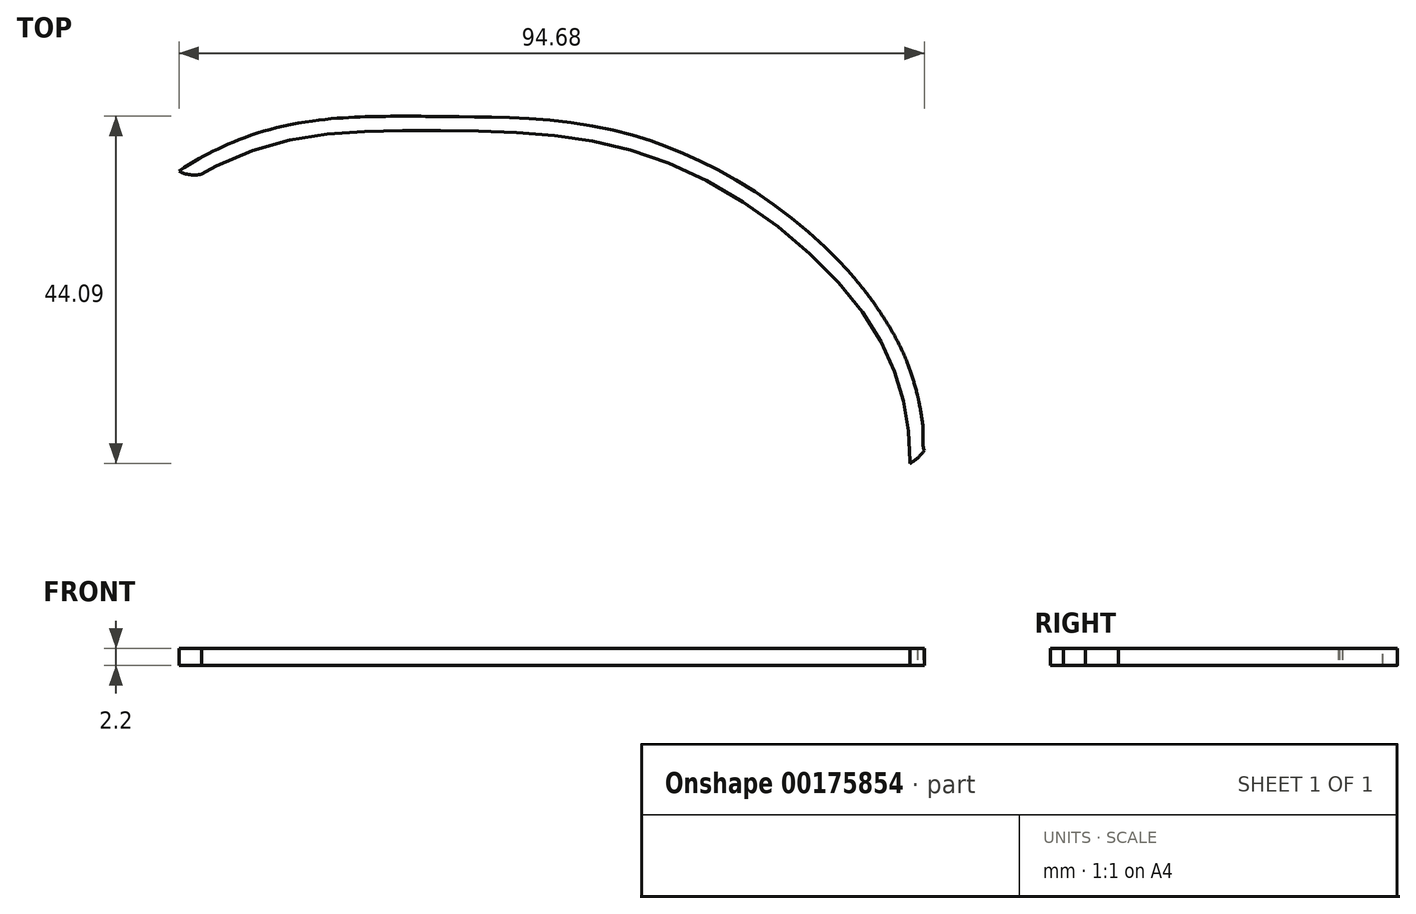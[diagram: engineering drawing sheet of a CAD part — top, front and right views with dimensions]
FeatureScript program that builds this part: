
annotation { "Feature Type Name" : "Feature", "Feature Type Description" : "" }
export const myFeature = defineFeature(function(context is Context, id is Id, definition is map)
    precondition{}
    {
        {
            var Q0;
            Q0=qCreatedBy(makeId("Top.planeOp"),FACE);
            var sketch = newSketch(context, id + "F0", { "sketchPlane" : qUnion([Q0])});
            skLineSegment(sketch, "E0.bottom", {"start": v(-2.66, 38.82) * mm, "end": v(-2.66, 38.82) * mm});
            skLineSegment(sketch, "E0.top", {"start": v(-2.66, -45.18) * mm, "end": v(-2.66, -45.18) * mm});
            skLineSegment(sketch, "E0.left", {"start": v(-62.96, 0) * mm, "end": v(-62.96, -6.37) * mm});
            skPoint(sketch, "E1", {"position": v(116.17, -2.24) * mm});
            skPoint(sketch, "E2", {"position": v(57.5, -3.18) * mm});
            skLineSegment(sketch, "E3", {"start": v(89.29, -3.18) * mm, "end": v(-122.26, -3.18) * mm, "construction": true});
            skFitSpline(sketch, "E4", {"points": [v(57.5, -3.18) * mm, v(51.83, 15.26) * mm, v(26.1, 35.01) * mm, v(-2.66, 38.82) * mm, v(-30.61, 34.33) * mm, v(-55.45, 11.12) * mm, v(-62.96, 0) * mm], "startDerivative": vector(0, 129.1) * mm, "endDerivative": vector(-47.35, -84.57) * mm});
            skFitSpline(sketch, "E5.MirrorCS", {"points": [v(57.5, -3.18) * mm, v(51.83, -21.63) * mm, v(26.1, -41.38) * mm, v(-2.66, -45.18) * mm, v(-30.61, -40.7) * mm, v(-55.45, -17.5) * mm, v(-62.96, -6.37) * mm], "startDerivative": vector(0, -129.1) * mm, "endDerivative": vector(-47.35, 84.57) * mm});
            skPoint(sketch, "E6.orphan", {"position": v(-62.96, 38.82) * mm});
            skPoint(sketch, "E7.orphan", {"position": v(57.63, 38.82) * mm});
            skPoint(sketch, "E8.orphan", {"position": v(57.37, -45.18) * mm});
            skFitSpline(sketch, "E9.0", {"points": [v(59.33, -3.18) * mm, v(59.33, -1.78) * mm, v(59.18, 1.03) * mm, v(58.46, 5.25) * mm, v(57.13, 9.45) * mm, v(55.46, 12.94) * mm, v(53.76, 15.71) * mm, v(51.79, 18.47) * mm, v(48.88, 21.87) * mm, v(44.8, 25.76) * mm, v(40.25, 29.38) * mm, v(35.35, 32.6) * mm, v(31.07, 34.9) * mm, v(27.59, 36.42) * mm, v(24.09, 37.72) * mm, v(19.72, 38.92) * mm, v(14.5, 39.84) * mm, v(9.33, 40.34) * mm, v(5.06, 40.53) * mm, v(1.66, 40.6) * mm, v(-0.88, 40.62) * mm, v(-3.4, 40.64) * mm, v(-5.95, 40.66) * mm, v(-8.5, 40.65) * mm, v(-11.9, 40.58) * mm, v(-16.2, 40.33) * mm, v(-21.36, 39.57) * mm, v(-25.65, 38.43) * mm, v(-29.06, 37.12) * mm, v(-31.6, 35.91) * mm, v(-34.11, 34.47) * mm, v(-37.38, 32.3) * mm, v(-41.32, 29.2) * mm, v(-45.76, 25.06) * mm, v(-49.84, 20.77) * mm, v(-53.49, 16.54) * mm, v(-56.63, 12.61) * mm, v(-59.17, 9.25) * mm, v(-61.95, 5.3) * mm, v(-63.54, 2.69) * mm, v(-64.55, 0.89) * mm]});
            skFitSpline(sketch, "E9.1", {"points": [v(59.33, -3.18) * mm, v(59.33, -4.59) * mm, v(59.18, -7.4) * mm, v(58.46, -11.62) * mm, v(57.13, -15.82) * mm, v(55.46, -19.3) * mm, v(53.76, -22.08) * mm, v(51.79, -24.84) * mm, v(48.88, -28.23) * mm, v(44.8, -32.13) * mm, v(40.25, -35.74) * mm, v(35.35, -38.97) * mm, v(31.07, -41.26) * mm, v(27.59, -42.78) * mm, v(24.09, -44.08) * mm, v(19.72, -45.29) * mm, v(14.5, -46.2) * mm, v(9.33, -46.7) * mm, v(5.06, -46.9) * mm, v(1.66, -46.96) * mm, v(-0.88, -47) * mm, v(-3.4, -47.01) * mm, v(-5.95, -47.03) * mm, v(-8.5, -47.02) * mm, v(-11.9, -46.95) * mm, v(-16.2, -46.7) * mm, v(-21.36, -45.94) * mm, v(-25.65, -44.8) * mm, v(-29.06, -43.48) * mm, v(-31.6, -42.28) * mm, v(-34.11, -40.84) * mm, v(-37.38, -38.67) * mm, v(-41.32, -35.56) * mm, v(-45.76, -31.43) * mm, v(-49.84, -27.13) * mm, v(-53.49, -22.9) * mm, v(-56.63, -18.98) * mm, v(-59.17, -15.62) * mm, v(-61.95, -11.67) * mm, v(-63.54, -9.05) * mm, v(-64.55, -7.26) * mm]});
            skLineSegment(sketch, "E10", {"start": v(-30.61, 34.33) * mm, "end": v(-31.63, 35.85) * mm});
            skLineSegment(sketch, "E11.MirrorCS", {"start": v(-30.61, -40.7) * mm, "end": v(-31.63, -42.22) * mm});
            skPoint(sketch, "E12.start.orphan", {"position": v(58.81, 3.06) * mm});
            skLineSegment(sketch, "E13.bottom", {"start": v(58.57, 4.32) * mm, "end": v(77.5, 4.32) * mm});
            skLineSegment(sketch, "E13.top", {"start": v(58.57, -10.68) * mm, "end": v(77.5, -10.68) * mm});
            skLineSegment(sketch, "E13.right", {"start": v(77.5, -0.18) * mm, "end": v(77.5, -6.18) * mm});
            skArc(sketch, "E14", {"start": v(77.5, -10.68) * mm, "mid": v(85, -3.18) * mm, "end": v(77.5, 4.32) * mm});
            skCircle(sketch, "E15", {"center": v(77.5, -3.18) * mm, "radius": 3 * mm});
            skArc(sketch, "E16", {"start": v(-33.05, 41.17) * mm, "mid": v(-37.18, 35.85) * mm, "end": v(-30.61, 34.33) * mm});
            skFitSpline(sketch, "E17", {"points": [v(-33.05, 41.17) * mm, v(-16.7, 40.2) * mm], "startDerivative": vector(14.5, -1.33) * mm, "endDerivative": vector(14.46, 1.6) * mm});
            skCircle(sketch, "E18", {"center": v(-33.41, 37.2) * mm, "radius": 1.5 * mm});
            skFitSpline(sketch, "E19.trimOffspring", {"points": [v(59.33, -3.18) * mm, v(59.33, -1.78) * mm, v(59.18, 1.03) * mm, v(58.46, 5.25) * mm, v(57.13, 9.45) * mm, v(55.46, 12.94) * mm, v(53.76, 15.71) * mm, v(51.79, 18.47) * mm, v(48.88, 21.87) * mm, v(44.8, 25.76) * mm, v(40.25, 29.38) * mm, v(35.35, 32.6) * mm, v(31.07, 34.9) * mm, v(27.59, 36.42) * mm, v(24.09, 37.72) * mm, v(19.72, 38.92) * mm, v(14.5, 39.84) * mm, v(9.33, 40.34) * mm, v(5.06, 40.53) * mm, v(1.66, 40.6) * mm, v(-0.88, 40.62) * mm, v(-3.4, 40.64) * mm, v(-5.95, 40.66) * mm, v(-8.5, 40.65) * mm, v(-11.9, 40.58) * mm, v(-16.2, 40.33) * mm, v(-21.36, 39.57) * mm, v(-25.65, 38.43) * mm, v(-29.06, 37.12) * mm, v(-31.6, 35.91) * mm, v(-34.11, 34.47) * mm, v(-37.38, 32.3) * mm, v(-41.32, 29.2) * mm, v(-45.76, 25.06) * mm, v(-49.84, 20.77) * mm, v(-53.49, 16.54) * mm, v(-56.63, 12.61) * mm, v(-59.17, 9.25) * mm, v(-61.95, 5.3) * mm, v(-63.54, 2.69) * mm, v(-64.55, 0.89) * mm, v(59.33, -3.18) * mm]});
            skCircle(sketch, "E20.MirrorC", {"center": v(-33.41, -43.56) * mm, "radius": 1.5 * mm});
            skArc(sketch, "E21.MirrorCS", {"start": v(-33.05, -47.54) * mm, "mid": v(-37.18, -42.22) * mm, "end": v(-30.61, -40.7) * mm});
            skFitSpline(sketch, "E22.MirrorCS", {"points": [v(-33.05, -47.54) * mm, v(-16.7, -46.57) * mm], "startDerivative": vector(14.5, 1.33) * mm, "endDerivative": vector(14.46, -1.6) * mm});
            skPoint(sketch, "E23.orphan", {"position": v(57.5, 4.32) * mm});
            skPoint(sketch, "E24.orphan", {"position": v(57.5, -10.68) * mm});
            skSolve(sketch);
        }
        {
            var Q0;
            Q0=makeQuery(id+"F0.imprint","IMPRINT",FACE,{"disambiguationData":[TD([[makeQuery(id+"F0.imprint","IMPRINT",EDGE,{"derivedFrom":sQuery(id+"F0.wireOp",EDGE,"E9.0")}),1.0]])]});
            extrude(context, id + "F1", {"entities" : qUnion([Q0]), "depth" : 2.2 * mm});
        }
        {
            var Q0;
            Q0=makeQuery(id+"F1.opExtrude","SWEPT_EDGE",EDGE,{"disambiguationData":[OSD([sQuery(id+"F0.wireOp",EDGE,"E9.1"),sQuery(id+"F0.wireOp",EDGE,"E13.top")])]});
            var Q1;
            Q1=makeQuery(id+"F1.opExtrude","SWEPT_EDGE",EDGE,{"disambiguationData":[OSD([sQuery(id+"F0.wireOp",EDGE,"E9.0"),sQuery(id+"F0.wireOp",EDGE,"E13.bottom")])]});
            fillet(context, id + "F2", {"entities" : qUnion([Q0, Q1]), "radius" : 5 * mm, "tangentPropagation" : true, "allowEdgeOverflow" : false});
        }
    });
